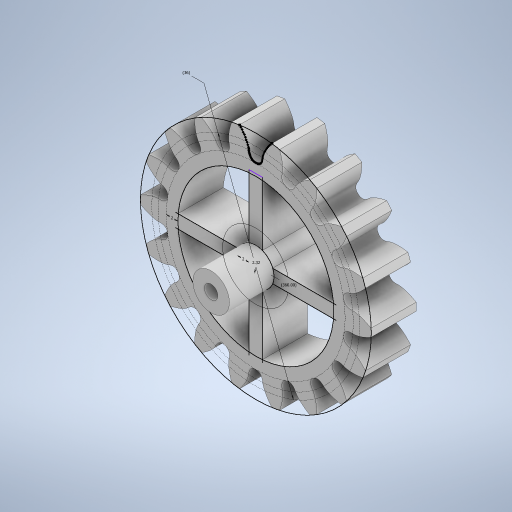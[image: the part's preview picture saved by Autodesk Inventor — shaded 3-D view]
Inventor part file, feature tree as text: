
AUTODESK INVENTOR PART (.ipt)
format: ipt  version: 2023 (Build 270158000, 158)  size: 434,688 bytes
history: native  units: mm
features: extrude x4, sketch x1, pattern_circular x1
ambient origin geometry x8: Origin, YZ Plane, XZ Plane, XY Plane, X Axis, Y Axis, Z Axis, Center Point
bodies: Solid1 (feature_tree)
feature tree (6):
  sketch  "Sketch1"  dims[d0=7.82mm d1=0.0mm d2=0.0mm d3=0.0mm d4=180.0mm d5=360.0deg d7=2.32mm d8=0.0mm d9=0.0mm d10=36.0mm d11=2.0mm d12=2.0mm d13=40.0mm d15=360.0deg d17=7.72mm d18=0.0mm d19=0.5mm d20=0.872665mm]
  extrude  "Extrusion1"  TaperAngle=0.0deg  [1 undecoded]
  extrude  "Extrusion2"  Depth=7.72mm TaperAngle=360.0deg
  pattern_circular  "Circular Pattern1"  [2 undecoded]
  extrude  "Extrusion3"  TaperAngle=0.0deg  [1 undecoded]
  extrude  "Extrusion4"  Depth=7.72mm
note: 4 required parameter values undecoded (feature->parameter linkage not recoverable at this tier; creation-order binding heuristic only, values carry confidence <= 0.55)
